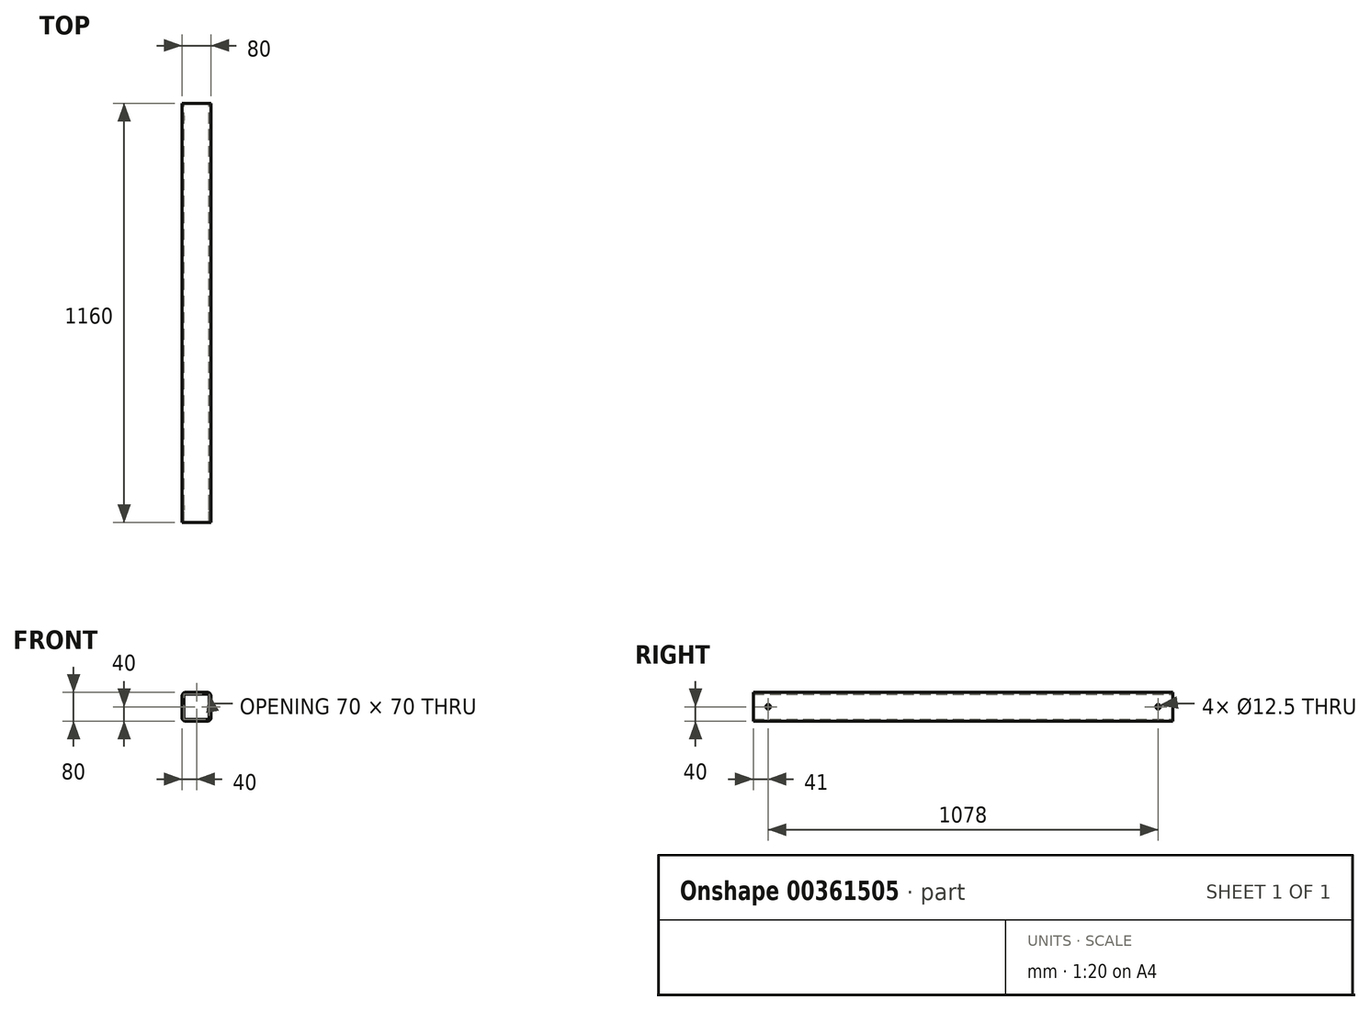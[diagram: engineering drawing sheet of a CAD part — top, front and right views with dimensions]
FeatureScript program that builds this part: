
annotation { "Feature Type Name" : "Feature", "Feature Type Description" : "" }
export const myFeature = defineFeature(function(context is Context, id is Id, definition is map)
    precondition{}
    {
        {
            var Q0;
            Q0=qCreatedBy(makeId("Front.planeOp"),FACE);
            var sketch = newSketch(context, id + "F0", { "sketchPlane" : qUnion([Q0])});
            skLineSegment(sketch, "E0.bottom", {"start": v(30, 40) * mm, "end": v(-30, 40) * mm});
            skLineSegment(sketch, "E0.top", {"start": v(30, -40) * mm, "end": v(-30, -40) * mm});
            skLineSegment(sketch, "E0.left", {"start": v(40, 30) * mm, "end": v(40, -30) * mm});
            skLineSegment(sketch, "E0.right", {"start": v(-40, 30) * mm, "end": v(-40, -30) * mm});
            skPoint(sketch, "E0.middle", {"position": v(0, 0) * mm});
            skPoint(sketch, "E1.visualSharp", {"position": v(-40, 40) * mm});
            skArc(sketch, "E1.filletArc", {"start": v(-30, 40) * mm, "mid": v(-37.07, 37.07) * mm, "end": v(-40, 30) * mm});
            skPoint(sketch, "E2.visualSharp", {"position": v(40, 40) * mm});
            skArc(sketch, "E2.filletArc", {"start": v(40, 30) * mm, "mid": v(37.07, 37.07) * mm, "end": v(30, 40) * mm});
            skPoint(sketch, "E3.visualSharp", {"position": v(40, -40) * mm});
            skArc(sketch, "E3.filletArc", {"start": v(30, -40) * mm, "mid": v(37.07, -37.07) * mm, "end": v(40, -30) * mm});
            skPoint(sketch, "E4.visualSharp", {"position": v(-40, -40) * mm});
            skArc(sketch, "E4.filletArc", {"start": v(-40, -30) * mm, "mid": v(-37.07, -37.07) * mm, "end": v(-30, -40) * mm});
            skArc(sketch, "E5.0", {"start": v(35, 30) * mm, "mid": v(33.54, 33.54) * mm, "end": v(30, 35) * mm});
            skLineSegment(sketch, "E5.1", {"start": v(35, 30) * mm, "end": v(35, -30) * mm});
            skLineSegment(sketch, "E5.2", {"start": v(30, 35) * mm, "end": v(-30, 35) * mm});
            skArc(sketch, "E5.3", {"start": v(30, -35) * mm, "mid": v(33.54, -33.54) * mm, "end": v(35, -30) * mm});
            skArc(sketch, "E5.4", {"start": v(-30, 35) * mm, "mid": v(-33.54, 33.54) * mm, "end": v(-35, 30) * mm});
            skLineSegment(sketch, "E5.5", {"start": v(-35, 30) * mm, "end": v(-35, -30) * mm});
            skArc(sketch, "E5.6", {"start": v(-35, -30) * mm, "mid": v(-33.54, -33.54) * mm, "end": v(-30, -35) * mm});
            skLineSegment(sketch, "E5.7", {"start": v(30, -35) * mm, "end": v(-30, -35) * mm});
            skSolve(sketch);
        }
        {
            var Q0;
            Q0 = qSketchRegion(id + "F0", true);
            extrude(context, id + "F1", {"entities" : qUnion([Q0]), "endBound" : BoundingType.SYMMETRIC, "depth" : 1160 * mm});
        }
        {
            var Q0;
            Q0=makeQuery(id+"F1.opExtrude","SWEPT_FACE",FACE,{"disambiguationData":[OSD([sQuery(id+"F0.wireOp",EDGE,"E0.left")])]});
            var sketch = newSketch(context, id + "F2", { "sketchPlane" : qUnion([Q0])});
            skLineSegment(sketch, "E6", {"start": v(-580, 0) * mm, "end": v(-539, 0) * mm, "construction": true});
            skPoint(sketch, "E6.endSnap0", {"position": v(-580, 0) * mm});
            skCircle(sketch, "E7", {"center": v(-539, 0) * mm, "radius": 6.25 * mm});
            skLineSegment(sketch, "E8", {"start": v(0, 0) * mm, "end": v(0, -30) * mm, "construction": true});
            skCircle(sketch, "E9.MirrorC", {"center": v(539, 0) * mm, "radius": 6.25 * mm});
            skSolve(sketch);
        }
        {
            var Q0;
            Q0 = qSketchRegion(id + "F2", true);
            extrude(context, id + "F3", {"entities" : qUnion([Q0]), "operationType" : NewBodyOperationType.REMOVE, "endBound" : BoundingType.THROUGH_ALL, "oppositeDirection" : true, "depth" : 25 * mm});
        }
    });
